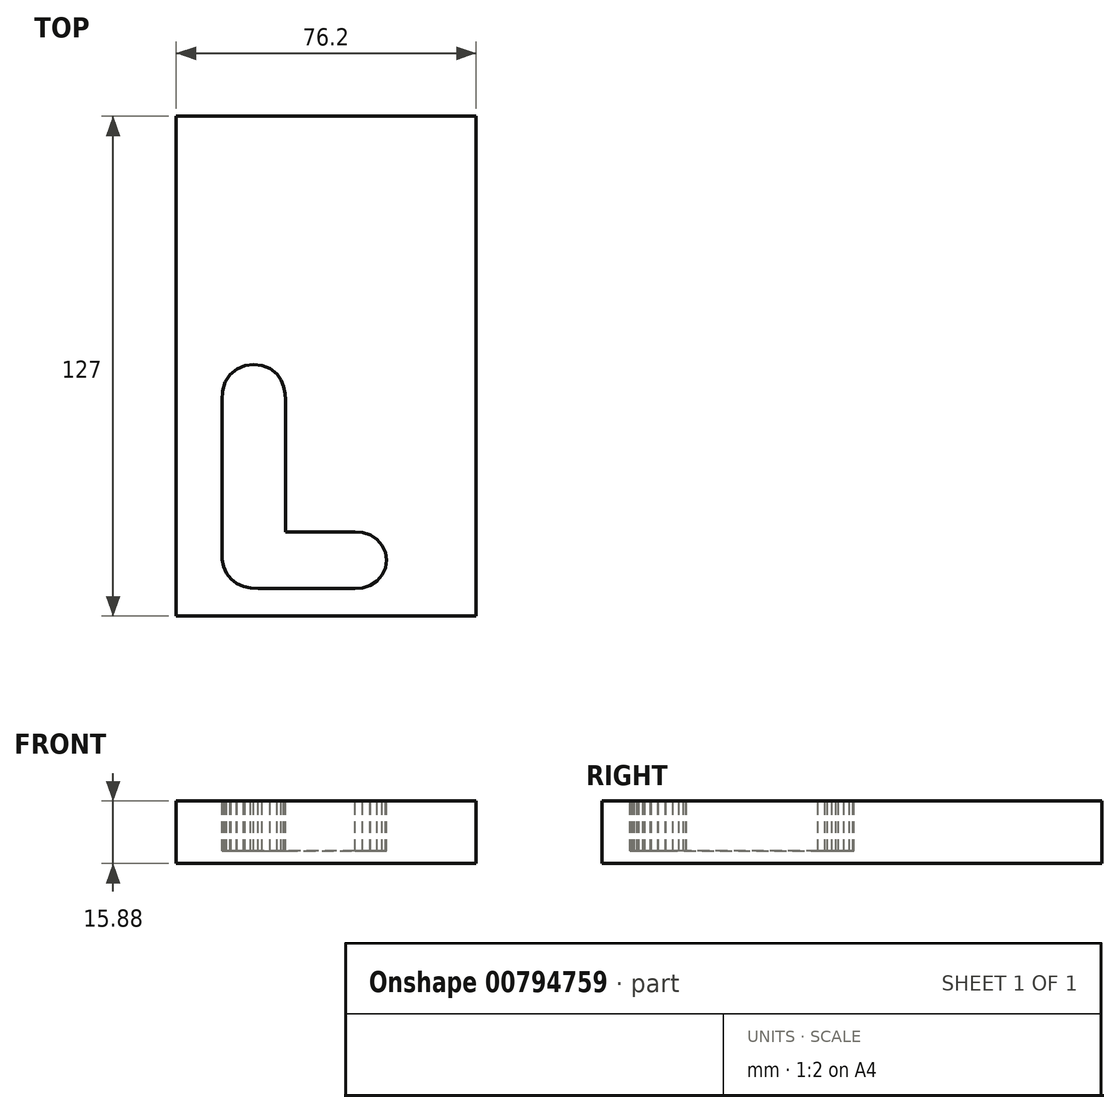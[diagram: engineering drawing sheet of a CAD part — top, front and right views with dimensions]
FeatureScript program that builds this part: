
annotation { "Feature Type Name" : "Feature", "Feature Type Description" : "" }
export const myFeature = defineFeature(function(context is Context, id is Id, definition is map)
    precondition{}
    {
        {
            var Q0;
            Q0=qCreatedBy(makeId("Top.planeOp"),FACE);
            var sketch = newSketch(context, id + "F0", { "sketchPlane" : qUnion([Q0])});
            skLineSegment(sketch, "E0.bottom", {"start": v(0, 0) * mm, "end": v(76.2, 0) * mm});
            skLineSegment(sketch, "E0.top", {"start": v(0, 127) * mm, "end": v(76.2, 127) * mm});
            skLineSegment(sketch, "E0.left", {"start": v(0, 0) * mm, "end": v(0, 127) * mm});
            skLineSegment(sketch, "E0.right", {"start": v(76.2, 0) * mm, "end": v(76.2, 127) * mm});
            skSolve(sketch);
        }
        {
            var Q0;
            Q0=makeQuery(id+"F0.imprint","IMPRINT",FACE,{"disambiguationData":[TD([[makeQuery(id+"F0.imprint","IMPRINT",EDGE,{"derivedFrom":sQuery(id+"F0.wireOp",EDGE,"E0.bottom")}),1.0]])]});
            extrude(context, id + "F1", {"entities" : qUnion([Q0]), "oppositeDirection" : true, "depth" : 15.88 * mm, "offsetDistance" : 25.4 * mm});
        }
        {
            var Q0;
            Q0=qCreatedBy(makeId("Top.planeOp"),FACE);
            var sketch = newSketch(context, id + "F2", { "sketchPlane" : qUnion([Q0])});
            skLineSegment(sketch, "E1.0", {"start": v(17.45, 63.7) * mm, "end": v(19.64, 63.97) * mm});
            skLineSegment(sketch, "E1.1", {"start": v(15.42, 62.85) * mm, "end": v(17.45, 63.7) * mm});
            skLineSegment(sketch, "E1.2", {"start": v(13.7, 61.4) * mm, "end": v(15.42, 62.85) * mm});
            skLineSegment(sketch, "E1.3", {"start": v(12.45, 59.46) * mm, "end": v(13.7, 61.4) * mm});
            skLineSegment(sketch, "E1.4", {"start": v(11.78, 57.2) * mm, "end": v(12.45, 59.46) * mm});
            skLineSegment(sketch, "E1.5", {"start": v(11.59, 54.9) * mm, "end": v(11.78, 57.2) * mm});
            skLineSegment(sketch, "E1.6", {"start": v(11.59, 16.2) * mm, "end": v(11.59, 54.9) * mm});
            skLineSegment(sketch, "E1.7", {"start": v(11.7, 14.37) * mm, "end": v(11.59, 16.2) * mm});
            skLineSegment(sketch, "E1.8", {"start": v(12.08, 12.57) * mm, "end": v(11.7, 14.37) * mm});
            skLineSegment(sketch, "E1.9", {"start": v(12.79, 10.88) * mm, "end": v(12.08, 12.57) * mm});
            skLineSegment(sketch, "E1.10", {"start": v(13.9, 9.4) * mm, "end": v(12.79, 10.88) * mm});
            skLineSegment(sketch, "E1.11", {"start": v(19.64, 63.97) * mm, "end": v(21.84, 63.7) * mm});
            skLineSegment(sketch, "E1.12", {"start": v(15.37, 8.27) * mm, "end": v(13.9, 9.4) * mm});
            skLineSegment(sketch, "E1.13", {"start": v(17.07, 7.54) * mm, "end": v(15.37, 8.27) * mm});
            skLineSegment(sketch, "E1.14", {"start": v(18.89, 7.16) * mm, "end": v(17.07, 7.54) * mm});
            skLineSegment(sketch, "E1.15", {"start": v(47.35, 21.25) * mm, "end": v(49.33, 20.63) * mm});
            skLineSegment(sketch, "E1.16", {"start": v(45.38, 21.43) * mm, "end": v(47.35, 21.25) * mm});
            skLineSegment(sketch, "E1.17", {"start": v(27.8, 21.43) * mm, "end": v(45.38, 21.43) * mm});
            skLineSegment(sketch, "E1.18", {"start": v(27.8, 54.85) * mm, "end": v(27.8, 21.43) * mm});
            skLineSegment(sketch, "E1.19", {"start": v(27.69, 56.62) * mm, "end": v(27.8, 54.85) * mm});
            skLineSegment(sketch, "E1.20", {"start": v(27.32, 58.38) * mm, "end": v(27.69, 56.62) * mm});
            skLineSegment(sketch, "E1.21", {"start": v(21.84, 63.7) * mm, "end": v(23.87, 62.87) * mm});
            skLineSegment(sketch, "E1.22", {"start": v(23.87, 62.87) * mm, "end": v(25.57, 61.5) * mm});
            skLineSegment(sketch, "E1.23", {"start": v(25.57, 61.5) * mm, "end": v(26.63, 60.02) * mm});
            skLineSegment(sketch, "E1.24", {"start": v(26.63, 60.02) * mm, "end": v(27.32, 58.38) * mm});
            skLineSegment(sketch, "E1.25", {"start": v(49.33, 20.63) * mm, "end": v(51.05, 19.5) * mm});
            skLineSegment(sketch, "E1.26", {"start": v(51.05, 19.5) * mm, "end": v(52.35, 17.96) * mm});
            skLineSegment(sketch, "E1.27", {"start": v(52.35, 17.96) * mm, "end": v(53.14, 16.16) * mm});
            skLineSegment(sketch, "E1.28", {"start": v(53.14, 16.16) * mm, "end": v(53.4, 14.2) * mm});
            skLineSegment(sketch, "E1.29", {"start": v(53.4, 14.2) * mm, "end": v(53.15, 12.25) * mm});
            skLineSegment(sketch, "E1.30", {"start": v(53.15, 12.25) * mm, "end": v(52.36, 10.43) * mm});
            skLineSegment(sketch, "E1.31", {"start": v(52.36, 10.43) * mm, "end": v(51.04, 8.9) * mm});
            skLineSegment(sketch, "E1.32", {"start": v(51.04, 8.9) * mm, "end": v(49.31, 7.8) * mm});
            skLineSegment(sketch, "E1.33", {"start": v(49.31, 7.8) * mm, "end": v(47.34, 7.21) * mm});
            skLineSegment(sketch, "E1.34", {"start": v(47.34, 7.21) * mm, "end": v(45.37, 7.05) * mm});
            skLineSegment(sketch, "E1.35", {"start": v(45.37, 7.05) * mm, "end": v(20.74, 7.05) * mm});
            skLineSegment(sketch, "E1.36", {"start": v(20.74, 7.05) * mm, "end": v(18.89, 7.16) * mm});
            skSolve(sketch);
        }
        {
            var Q0;
            Q0 = qSketchRegion(id + "F2", true);
            extrude(context, id + "F3", {"entities" : qUnion([Q0]), "operationType" : NewBodyOperationType.REMOVE, "oppositeDirection" : true, "depth" : 12.7 * mm, "offsetDistance" : 25.4 * mm});
        }
    });
